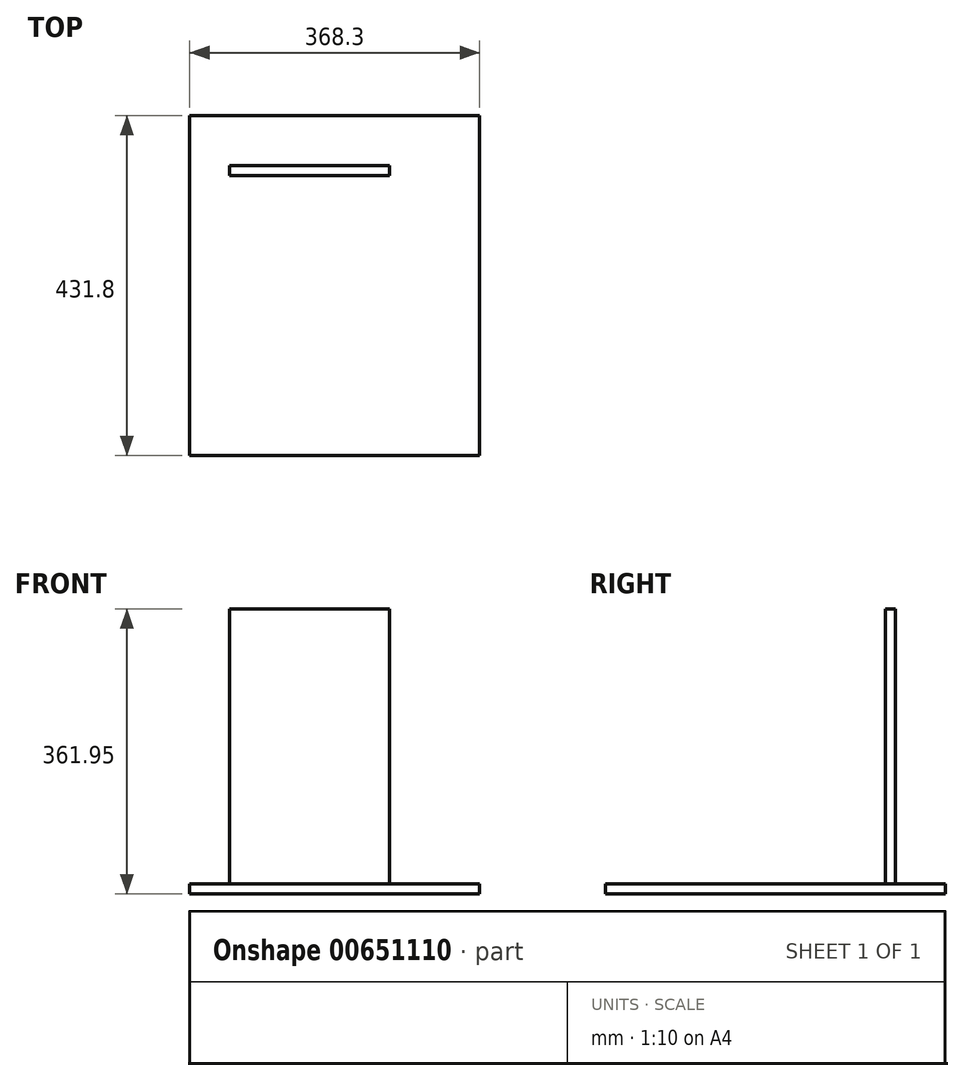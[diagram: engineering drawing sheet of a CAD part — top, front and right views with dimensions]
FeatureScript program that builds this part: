
annotation { "Feature Type Name" : "Feature", "Feature Type Description" : "" }
export const myFeature = defineFeature(function(context is Context, id is Id, definition is map)
    precondition{}
    {
        {
            var Q0;
            Q0=qCreatedBy(makeId("Top.planeOp"),FACE);
            var sketch = newSketch(context, id + "F0", { "sketchPlane" : qUnion([Q0])});
            skLineSegment(sketch, "E0.bottom", {"start": v(-184.15, 215.9) * mm, "end": v(184.15, 215.9) * mm});
            skLineSegment(sketch, "E0.top", {"start": v(-184.15, -215.9) * mm, "end": v(184.15, -215.9) * mm});
            skLineSegment(sketch, "E0.left", {"start": v(-184.15, 215.9) * mm, "end": v(-184.15, -215.9) * mm});
            skLineSegment(sketch, "E0.right", {"start": v(184.15, 215.9) * mm, "end": v(184.15, -215.9) * mm});
            skLineSegment(sketch, "E1", {"start": v(-184.15, 215.9) * mm, "end": v(184.15, -215.9) * mm, "construction": true});
            skSolve(sketch);
        }
        {
            var Q0;
            Q0=makeQuery(id+"F0.imprint","IMPRINT",FACE,{"disambiguationData":[TD([[makeQuery(id+"F0.imprint","IMPRINT",EDGE,{"derivedFrom":sQuery(id+"F0.wireOp",EDGE,"E0.bottom")}),-1.0]])]});
            extrude(context, id + "F1", {"entities" : qUnion([Q0]), "depth" : 12.7 * mm, "offsetDistance" : 25.4 * mm});
        }
        {
            var Q0;
            Q0=makeQuery(id+"F1.opExtrude","CAP_FACE",FACE,{"disambiguationData":[OSD([sQuery(id+"F0.wireOp",EDGE,"E0.bottom"),sQuery(id+"F0.wireOp",EDGE,"E0.top"),sQuery(id+"F0.wireOp",EDGE,"E0.left"),sQuery(id+"F0.wireOp",EDGE,"E0.right")])],"isStart":false});
            var sketch = newSketch(context, id + "F2", { "sketchPlane" : qUnion([Q0])});
            skLineSegment(sketch, "E2.bottom", {"start": v(-133.35, 152.4) * mm, "end": v(69.85, 152.4) * mm});
            skLineSegment(sketch, "E2.top", {"start": v(-133.35, 139.7) * mm, "end": v(69.85, 139.7) * mm});
            skLineSegment(sketch, "E2.left", {"start": v(-133.35, 152.4) * mm, "end": v(-133.35, 139.7) * mm});
            skLineSegment(sketch, "E2.right", {"start": v(69.85, 152.4) * mm, "end": v(69.85, 139.7) * mm});
            skSolve(sketch);
        }
        {
            var Q0;
            Q0 = qSketchRegion(id + "F2", true);
            extrude(context, id + "F3", {"entities" : qUnion([Q0]), "operationType" : NewBodyOperationType.ADD, "depth" : 349.25 * mm, "offsetDistance" : 25.4 * mm});
        }
        {
            var Q0;
            Q0=makeQuery(id+"F1.opExtrude","CAP_FACE",FACE,{"disambiguationData":[OSD([sQuery(id+"F0.wireOp",EDGE,"E0.bottom"),sQuery(id+"F0.wireOp",EDGE,"E0.top"),sQuery(id+"F0.wireOp",EDGE,"E0.left"),sQuery(id+"F0.wireOp",EDGE,"E0.right")])],"isStart":false});
            var sketch = newSketch(context, id + "F4", { "sketchPlane" : qUnion([Q0])});
            skPoint(sketch, "E3", {"position": v(-133.35, -215.9) * mm});
            skSolve(sketch);
        }
        {
            var Q0;
            Q0=qCreatedBy(makeId("Front.planeOp"),FACE);
            cPlane(context, id + "F5", {"entities" : qUnion([Q0]), "cplaneType" : CPlaneType.OFFSET, "offset" : 76.2 * mm, "width" : 152.4 * mm, "height" : 152.4 * mm});
        }
        {
            var Q0;
            Q0=qCreatedBy(id+"F5.planeOp",FACE);
            var sketch = newSketch(context, id + "F6", { "sketchPlane" : qUnion([Q0])});
            skPoint(sketch, "E4", {"position": v(88.9, 63.5) * mm});
            skSolve(sketch);
        }
    });
